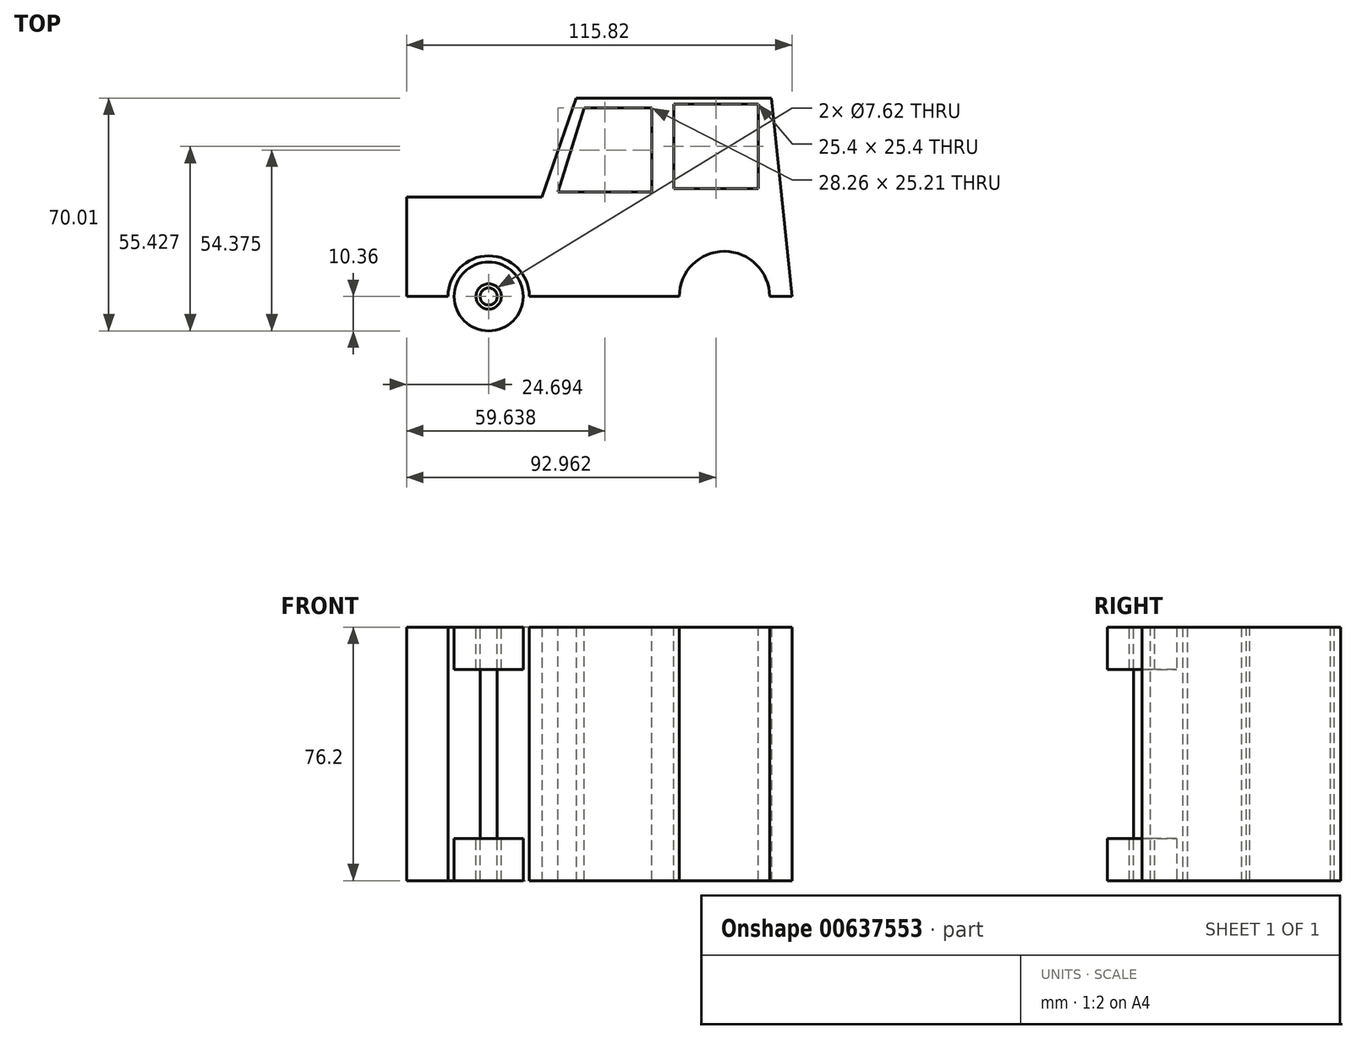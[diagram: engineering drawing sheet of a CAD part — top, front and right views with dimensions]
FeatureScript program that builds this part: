
annotation { "Feature Type Name" : "Feature", "Feature Type Description" : "" }
export const myFeature = defineFeature(function(context is Context, id is Id, definition is map)
    precondition{}
    {
        {
            var Q0;
            Q0=qCreatedBy(makeId("Top.planeOp"),FACE);
            var sketch = newSketch(context, id + "F0", { "sketchPlane" : qUnion([Q0])});
            skLineSegment(sketch, "E0", {"start": v(-50.95, 0) * mm, "end": v(-50.95, 29.89) * mm});
            skLineSegment(sketch, "E1", {"start": v(-50.95, 29.89) * mm, "end": v(-10.28, 29.89) * mm});
            skLineSegment(sketch, "E2", {"start": v(-10.28, 29.89) * mm, "end": v(0, 59.65) * mm});
            skLineSegment(sketch, "E3", {"start": v(0, 59.65) * mm, "end": v(58.67, 59.65) * mm});
            skLineSegment(sketch, "E4", {"start": v(58.67, 59.65) * mm, "end": v(64.87, 0) * mm});
            skLineSegment(sketch, "E5", {"start": v(64.87, 0) * mm, "end": v(-50.95, 0) * mm});
            skSolve(sketch);
        }
        {
            var Q0;
            Q0=makeQuery(id+"F0.imprint","IMPRINT",FACE,{"disambiguationData":[TD([[makeQuery(id+"F0.imprint","IMPRINT",EDGE,{"derivedFrom":sQuery(id+"F0.wireOp",EDGE,"E0")}),-1.0]])]});
            extrude(context, id + "F1", {"entities" : qUnion([Q0]), "endBound" : BoundingType.SYMMETRIC, "depth" : 76.2 * mm, "offsetDistance" : 25.4 * mm});
        }
        {
            var Q0;
            Q0=makeQuery(id+"F1.opExtrude","CAP_FACE",FACE,{"disambiguationData":[OSD([sQuery(id+"F0.wireOp",EDGE,"E0"),sQuery(id+"F0.wireOp",EDGE,"E1"),sQuery(id+"F0.wireOp",EDGE,"E2"),sQuery(id+"F0.wireOp",EDGE,"E3"),sQuery(id+"F0.wireOp",EDGE,"E4"),sQuery(id+"F0.wireOp",EDGE,"E5")])],"isStart":true});
            var sketch = newSketch(context, id + "F2", { "sketchPlane" : qUnion([Q0])});
            skCircle(sketch, "E6", {"center": v(-26.26, 0) * mm, "radius": 12.2 * mm});
            skSolve(sketch);
        }
        {
            var Q0;
            {var subQ0=sQuery(id+"F2.wireOp",EDGE,"E6");var subQ1=makeQuery(id+"F1.opExtrude","CAP_EDGE",EDGE,{"disambiguationData":[OSD([sQuery(id+"F0.wireOp",EDGE,"E5")])],"isStart":true});var subQ2=makeQuery(id+"F2.imprint","INTERSECT",VERTEX,{"disambiguationData":[OD(0.0)],"derivedFrom":[subQ1,subQ0]});Q0=makeQuery(id+"F2.imprint","IMPRINT",FACE,{"disambiguationData":[TD([[makeQuery(id+"F2.imprint","IMPRINT",EDGE,{"disambiguationData":[TD([[subQ2,1.0]])],"derivedFrom":subQ0}),1.0]])]});}
            var Q1;
            {var subQ0=sQuery(id+"F2.wireOp",EDGE,"E6");var subQ1=makeQuery(id+"F1.opExtrude","CAP_EDGE",EDGE,{"disambiguationData":[OSD([sQuery(id+"F0.wireOp",EDGE,"E5")])],"isStart":true});var subQ2=makeQuery(id+"F2.imprint","INTERSECT",VERTEX,{"disambiguationData":[OD(0.0)],"derivedFrom":[subQ1,subQ0]});Q1=makeQuery(id+"F2.imprint","IMPRINT",FACE,{"disambiguationData":[TD([[makeQuery(id+"F2.imprint","IMPRINT",EDGE,{"disambiguationData":[TD([[subQ2,-1.0]])],"derivedFrom":subQ0}),1.0]])]});}
            extrude(context, id + "F3", {"entities" : qUnion([Q0, Q1]), "operationType" : NewBodyOperationType.REMOVE, "oppositeDirection" : true, "depth" : 101.6 * mm, "offsetDistance" : 25.4 * mm});
        }
        {
            var Q0;
            Q0=makeQuery(id+"F1.opExtrude","CAP_FACE",FACE,{"disambiguationData":[OSD([sQuery(id+"F0.wireOp",EDGE,"E0"),sQuery(id+"F0.wireOp",EDGE,"E1"),sQuery(id+"F0.wireOp",EDGE,"E2"),sQuery(id+"F0.wireOp",EDGE,"E3"),sQuery(id+"F0.wireOp",EDGE,"E4"),sQuery(id+"F0.wireOp",EDGE,"E5")])],"isStart":true});
            var sketch = newSketch(context, id + "F4", { "sketchPlane" : qUnion([Q0])});
            skCircle(sketch, "E7", {"center": v(44.59, 0) * mm, "radius": 13.57 * mm});
            skSolve(sketch);
        }
        {
            var Q0;
            {var subQ0=sQuery(id+"F4.wireOp",EDGE,"E7");var subQ1=sQuery(id+"F0.wireOp",EDGE,"E5");var subQ2=sQuery(id+"F0.wireOp",EDGE,"E4");var subQ3=makeQuery(id+"F3.boolean.opBoolean","SPLIT",EDGE,{"disambiguationData":[TD([makeQuery(id+"F1.opExtrude","SWEPT_FACE",FACE,{"disambiguationData":[OSD([subQ2])]})])],"derivedFrom":makeQuery(id+"F1.opExtrude","CAP_EDGE",EDGE,{"disambiguationData":[OSD([subQ1])],"isStart":true})});var subQ4=makeQuery(id+"F4.imprint","INTERSECT",VERTEX,{"disambiguationData":[OD(0.0)],"derivedFrom":[subQ3,subQ0]});Q0=makeQuery(id+"F4.imprint","IMPRINT",FACE,{"disambiguationData":[TD([[makeQuery(id+"F4.imprint","IMPRINT",EDGE,{"disambiguationData":[TD([[subQ4,-1.0]])],"derivedFrom":subQ0}),1.0]])]});}
            var Q1;
            {var subQ0=sQuery(id+"F4.wireOp",EDGE,"E7");var subQ1=sQuery(id+"F0.wireOp",EDGE,"E5");var subQ2=sQuery(id+"F0.wireOp",EDGE,"E4");var subQ3=makeQuery(id+"F3.boolean.opBoolean","SPLIT",EDGE,{"disambiguationData":[TD([makeQuery(id+"F1.opExtrude","SWEPT_FACE",FACE,{"disambiguationData":[OSD([subQ2])]})])],"derivedFrom":makeQuery(id+"F1.opExtrude","CAP_EDGE",EDGE,{"disambiguationData":[OSD([subQ1])],"isStart":true})});var subQ4=makeQuery(id+"F4.imprint","INTERSECT",VERTEX,{"disambiguationData":[OD(0.0)],"derivedFrom":[subQ3,subQ0]});Q1=makeQuery(id+"F4.imprint","IMPRINT",FACE,{"disambiguationData":[TD([[makeQuery(id+"F4.imprint","IMPRINT",EDGE,{"disambiguationData":[TD([[subQ4,1.0]])],"derivedFrom":subQ0}),1.0]])]});}
            extrude(context, id + "F5", {"entities" : qUnion([Q0, Q1]), "operationType" : NewBodyOperationType.REMOVE, "oppositeDirection" : true, "depth" : 101.6 * mm, "offsetDistance" : 25.4 * mm});
        }
        {
            var Q0;
            Q0=qCreatedBy(makeId("Top.planeOp"),FACE);
            var sketch = newSketch(context, id + "F6", { "sketchPlane" : qUnion([Q0])});
            skCircle(sketch, "E8", {"center": v(-26.26, 0) * mm, "radius": 10.36 * mm});
            skCircle(sketch, "E9", {"center": v(44.97, 0) * mm, "radius": 10.6 * mm});
            skSolve(sketch);
        }
        {
            var Q0;
            Q0=makeQuery(id+"F6.imprint","IMPRINT",FACE,{"disambiguationData":[TD([[makeQuery(id+"F6.imprint","IMPRINT",EDGE,{"derivedFrom":sQuery(id+"F6.wireOp",EDGE,"E8")}),1.0]])]});
            var Q1;
            Q1=makeQuery(id+"F6.imprint","IMPRINT",FACE,{"disambiguationData":[TD([[makeQuery(id+"F6.imprint","IMPRINT",EDGE,{"derivedFrom":sQuery(id+"F6.wireOp",EDGE,"E9")}),1.0]])]});
            extrude(context, id + "F7", {"entities" : qUnion([Q0, Q1]), "endBound" : BoundingType.SYMMETRIC, "depth" : 76.2 * mm, "offsetDistance" : 25.4 * mm});
        }
        {
            var Q0;
            Q0=makeQuery(id+"F7.opExtrude","CAP_FACE",FACE,{"disambiguationData":[OSD([sQuery(id+"F6.wireOp",EDGE,"E8")])],"isStart":false});
            var sketch = newSketch(context, id + "F8", { "sketchPlane" : qUnion([Q0])});
            skCircle(sketch, "E10", {"center": v(-26.26, 0) * mm, "radius": 3.81 * mm});
            skSolve(sketch);
        }
        {
            var Q0;
            Q0=makeQuery(id+"F7.opExtrude","CAP_FACE",FACE,{"disambiguationData":[OSD([sQuery(id+"F6.wireOp",EDGE,"E9")])],"isStart":false});
            var sketch = newSketch(context, id + "F9", { "sketchPlane" : qUnion([Q0])});
            skCircle(sketch, "E11", {"center": v(44.97, 0) * mm, "radius": 3.81 * mm});
            skSolve(sketch);
        }
        {
            var Q0;
            Q0=makeQuery(id+"F8.imprint","IMPRINT",FACE,{"disambiguationData":[TD([[makeQuery(id+"F8.imprint","IMPRINT",EDGE,{"derivedFrom":sQuery(id+"F8.wireOp",EDGE,"E10")}),1.0]])]});
            var Q1;
            Q1=makeQuery(id+"F9.imprint","IMPRINT",FACE,{"disambiguationData":[TD([[makeQuery(id+"F9.imprint","IMPRINT",EDGE,{"derivedFrom":sQuery(id+"F9.wireOp",EDGE,"E11")}),1.0]])]});
            extrude(context, id + "F10", {"entities" : qUnion([Q0, Q1]), "operationType" : NewBodyOperationType.REMOVE, "oppositeDirection" : true, "depth" : 101.6 * mm, "offsetDistance" : 25.4 * mm});
        }
        {
            var Q0;
            Q0=makeQuery(id+"F7.opExtrude","CAP_FACE",FACE,{"disambiguationData":[OSD([sQuery(id+"F6.wireOp",EDGE,"E9")])],"isStart":true});
            var sketch = newSketch(context, id + "F11", { "sketchPlane" : qUnion([Q0])});
            skCircle(sketch, "E12", {"center": v(44.97, 0) * mm, "radius": 3.81 * mm});
            skSolve(sketch);
        }
        {
            var Q0;
            Q0=makeQuery(id+"F11.imprint","IMPRINT",FACE,{"disambiguationData":[TD([[makeQuery(id+"F11.imprint","IMPRINT",EDGE,{"derivedFrom":sQuery(id+"F11.wireOp",EDGE,"E12")}),1.0]])]});
            extrude(context, id + "F12", {"entities" : qUnion([Q0]), "operationType" : NewBodyOperationType.REMOVE, "oppositeDirection" : true, "depth" : 76.2 * mm, "offsetDistance" : 25.4 * mm});
        }
        {
            var Q0;
            Q0=makeQuery(id+"F7.opExtrude","CAP_FACE",FACE,{"disambiguationData":[OSD([sQuery(id+"F6.wireOp",EDGE,"E8")])],"isStart":false});
            var sketch = newSketch(context, id + "F13", { "sketchPlane" : qUnion([Q0])});
            skCircle(sketch, "E13", {"center": v(-26.26, 0) * mm, "radius": 2.57 * mm});
            skSolve(sketch);
        }
        {
            var Q0;
            Q0=makeQuery(id+"F7.opExtrude","CAP_FACE",FACE,{"disambiguationData":[OSD([sQuery(id+"F6.wireOp",EDGE,"E9")])],"isStart":false});
            var sketch = newSketch(context, id + "F14", { "sketchPlane" : qUnion([Q0])});
            skCircle(sketch, "E14", {"center": v(44.97, 0) * mm, "radius": 2.87 * mm});
            skSolve(sketch);
        }
        {
            var Q0;
            Q0=makeQuery(id+"F1.opExtrude","CAP_FACE",FACE,{"disambiguationData":[OSD([sQuery(id+"F0.wireOp",EDGE,"E0"),sQuery(id+"F0.wireOp",EDGE,"E1"),sQuery(id+"F0.wireOp",EDGE,"E2"),sQuery(id+"F0.wireOp",EDGE,"E3"),sQuery(id+"F0.wireOp",EDGE,"E4"),sQuery(id+"F0.wireOp",EDGE,"E5")])],"isStart":false});
            var sketch = newSketch(context, id + "F15", { "sketchPlane" : qUnion([Q0])});
            skLineSegment(sketch, "E15", {"start": v(-5.44, 31.41) * mm, "end": v(2.39, 56.62) * mm});
            skLineSegment(sketch, "E16", {"start": v(2.39, 56.62) * mm, "end": v(22.82, 56.62) * mm});
            skLineSegment(sketch, "E17", {"start": v(-5.44, 31.41) * mm, "end": v(0, 31.41) * mm});
            skLineSegment(sketch, "E18", {"start": v(22.82, 56.62) * mm, "end": v(22.82, 31.41) * mm});
            skLineSegment(sketch, "E19", {"start": v(22.82, 31.41) * mm, "end": v(0, 31.41) * mm});
            skSolve(sketch);
        }
        {
            var Q0;
            Q0=makeQuery(id+"F15.imprint","IMPRINT",FACE,{"disambiguationData":[TD([[makeQuery(id+"F15.imprint","IMPRINT",EDGE,{"derivedFrom":sQuery(id+"F15.wireOp",EDGE,"E15")}),-1.0]])]});
            extrude(context, id + "F16", {"entities" : qUnion([Q0]), "operationType" : NewBodyOperationType.REMOVE, "oppositeDirection" : true, "depth" : 76.2 * mm, "offsetDistance" : 25.4 * mm});
        }
        {
            var Q0;
            Q0=makeQuery(id+"F1.opExtrude","CAP_FACE",FACE,{"disambiguationData":[OSD([sQuery(id+"F0.wireOp",EDGE,"E0"),sQuery(id+"F0.wireOp",EDGE,"E1"),sQuery(id+"F0.wireOp",EDGE,"E2"),sQuery(id+"F0.wireOp",EDGE,"E3"),sQuery(id+"F0.wireOp",EDGE,"E4"),sQuery(id+"F0.wireOp",EDGE,"E5")])],"isStart":false});
            var sketch = newSketch(context, id + "F17", { "sketchPlane" : qUnion([Q0])});
            skLineSegment(sketch, "E20", {"start": v(29.31, 57.77) * mm, "end": v(29.31, 32.37) * mm});
            skLineSegment(sketch, "E21", {"start": v(29.31, 32.37) * mm, "end": v(54.71, 32.37) * mm});
            skLineSegment(sketch, "E22", {"start": v(54.71, 32.37) * mm, "end": v(54.71, 57.77) * mm});
            skLineSegment(sketch, "E23", {"start": v(54.71, 57.77) * mm, "end": v(29.31, 57.77) * mm});
            skSolve(sketch);
        }
        {
            var Q0;
            Q0=makeQuery(id+"F17.imprint","IMPRINT",FACE,{"disambiguationData":[TD([[makeQuery(id+"F17.imprint","IMPRINT",EDGE,{"derivedFrom":sQuery(id+"F17.wireOp",EDGE,"E20")}),1.0]])]});
            extrude(context, id + "F18", {"entities" : qUnion([Q0]), "operationType" : NewBodyOperationType.REMOVE, "oppositeDirection" : true, "depth" : 76.2 * mm, "offsetDistance" : 25.4 * mm});
        }
        {
            var Q0;
            Q0=qCreatedBy(makeId("Top.planeOp"),FACE);
            var sketch = newSketch(context, id + "F19", { "sketchPlane" : qUnion([Q0])});
            skCircle(sketch, "E24", {"center": v(-26.26, 0) * mm, "radius": 10.55 * mm});
            skSolve(sketch);
        }
        {
            var Q0;
            Q0 = qSketchRegion(id + "F19", true);
            extrude(context, id + "F20", {"entities" : qUnion([Q0]), "operationType" : NewBodyOperationType.REMOVE, "endBound" : BoundingType.SYMMETRIC, "oppositeDirection" : true, "depth" : 50.8 * mm, "offsetDistance" : 25.4 * mm});
        }
        {
            var Q0;
            Q0=qCreatedBy(makeId("Top.planeOp"),FACE);
            var sketch = newSketch(context, id + "F21", { "sketchPlane" : qUnion([Q0])});
            skCircle(sketch, "E25", {"center": v(44.97, 0) * mm, "radius": 11.45 * mm});
            skSolve(sketch);
        }
        {
            var Q0;
            Q0 = qSketchRegion(id + "F21", true);
            extrude(context, id + "F22", {"entities" : qUnion([Q0]), "operationType" : NewBodyOperationType.REMOVE, "endBound" : BoundingType.SYMMETRIC, "depth" : 50.8 * mm, "offsetDistance" : 25.4 * mm});
        }
        {
            var Q0;
            Q0=makeQuery(id+"F13.imprint","IMPRINT",FACE,{"disambiguationData":[TD([[makeQuery(id+"F13.imprint","IMPRINT",EDGE,{"derivedFrom":sQuery(id+"F13.wireOp",EDGE,"E13")}),1.0]])]});
            var Q1;
            Q1=makeQuery(id+"F14.imprint","IMPRINT",FACE,{"disambiguationData":[TD([[makeQuery(id+"F14.imprint","IMPRINT",EDGE,{"derivedFrom":sQuery(id+"F14.wireOp",EDGE,"E14")}),1.0]])]});
            extrude(context, id + "F23", {"entities" : qUnion([Q0, Q1]), "oppositeDirection" : true, "depth" : 76.2 * mm, "offsetDistance" : 25.4 * mm});
        }
    });
